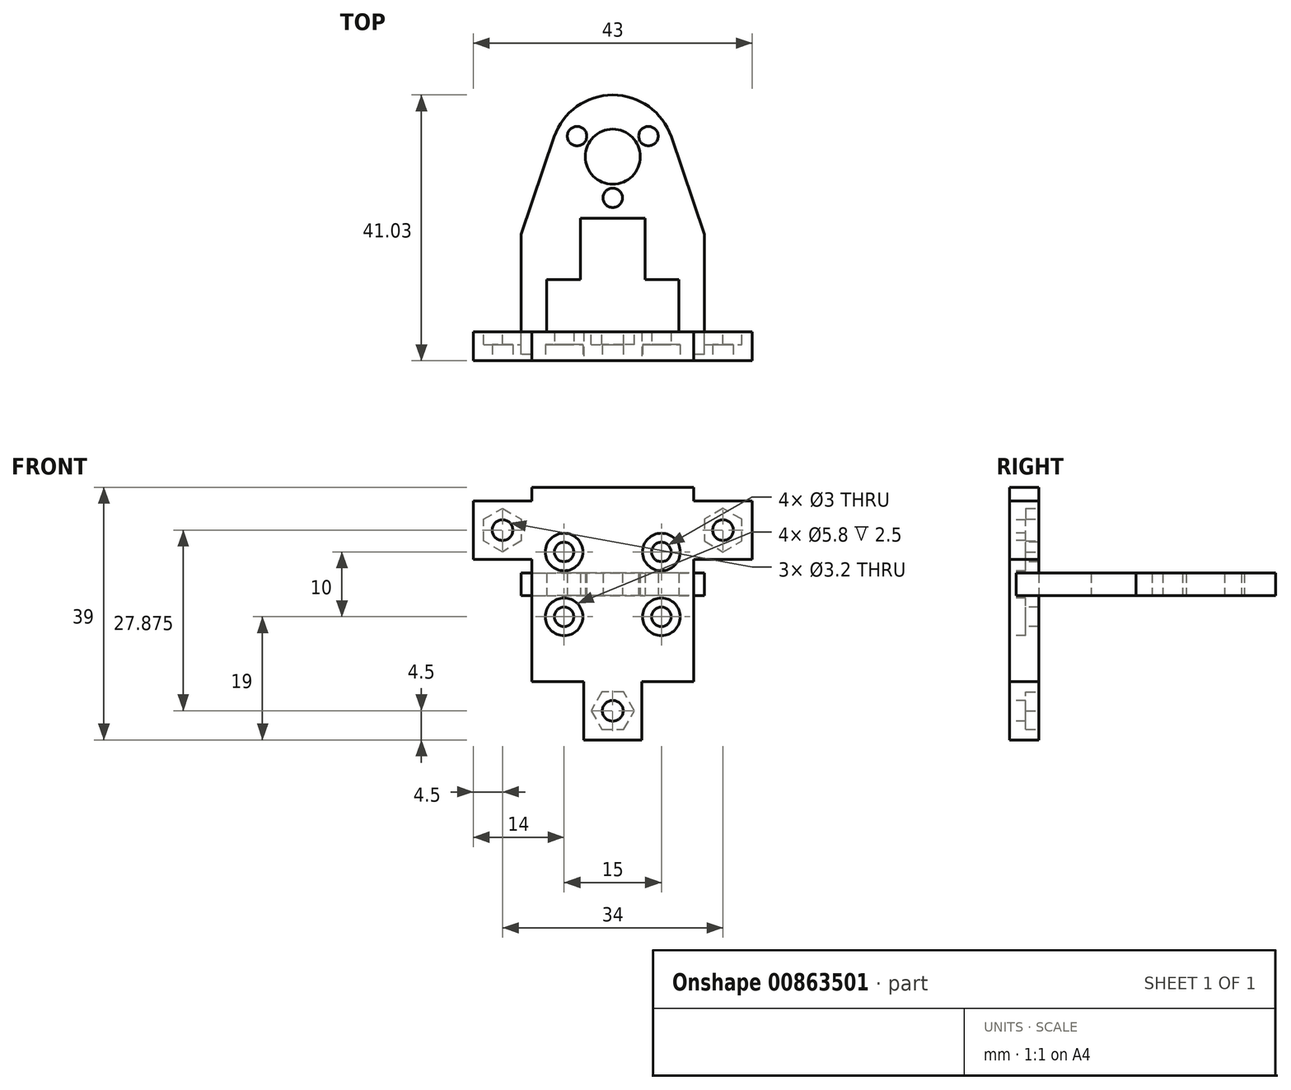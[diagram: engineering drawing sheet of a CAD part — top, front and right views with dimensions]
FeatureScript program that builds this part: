
annotation { "Feature Type Name" : "Feature", "Feature Type Description" : "" }
export const myFeature = defineFeature(function(context is Context, id is Id, definition is map)
    precondition{}
    {
        {
            var Q0;
            Q0=qCreatedBy(makeId("Top.planeOp"),FACE);
            var sketch = newSketch(context, id + "F0", { "sketchPlane" : qUnion([Q0])});
            skCircle(sketch, "E0", {"center": v(0, 0) * mm, "radius": 4.25 * mm});
            skCircle(sketch, "E1", {"center": v(0, -6.35) * mm, "radius": 1.5 * mm});
            skCircle(sketch, "E2.1.0", {"center": v(5.5, 3.17) * mm, "radius": 1.5 * mm});
            skCircle(sketch, "E2.2.0", {"center": v(-5.5, 3.18) * mm, "radius": 1.5 * mm});
            skLineSegment(sketch, "E3", {"start": v(0, -30.5) * mm, "end": v(14.1, -30.5) * mm});
            skLineSegment(sketch, "E4", {"start": v(14.1, -30.5) * mm, "end": v(14.1, -12) * mm});
            skCircle(sketch, "E5", {"center": v(0, 0) * mm, "radius": 9.53 * mm, "construction": true});
            skLineSegment(sketch, "E6", {"start": v(14.1, -12) * mm, "end": v(9.03, 3.04) * mm});
            skLineSegment(sketch, "E7", {"start": v(0, -27) * mm, "end": v(10.2, -27) * mm});
            skLineSegment(sketch, "E8", {"start": v(10.2, -27) * mm, "end": v(10.2, -18.95) * mm});
            skLineSegment(sketch, "E9", {"start": v(10.2, -18.95) * mm, "end": v(5, -18.95) * mm});
            skLineSegment(sketch, "E10", {"start": v(5, -18.95) * mm, "end": v(5, -9.52) * mm});
            skLineSegment(sketch, "E11", {"start": v(5, -9.52) * mm, "end": v(0, -9.52) * mm});
            skLineSegment(sketch, "E12.MirrorCS", {"start": v(-14.1, -12) * mm, "end": v(-9.03, 3.04) * mm});
            skLineSegment(sketch, "E13.MirrorCS", {"start": v(-5, -18.95) * mm, "end": v(-5, -9.52) * mm});
            skLineSegment(sketch, "E14.MirrorCS", {"start": v(-5, -9.52) * mm, "end": v(0, -9.52) * mm});
            skLineSegment(sketch, "E15.MirrorCS", {"start": v(-10.2, -18.95) * mm, "end": v(-5, -18.95) * mm});
            skLineSegment(sketch, "E16.MirrorCS", {"start": v(-10.2, -27) * mm, "end": v(-10.2, -18.95) * mm});
            skLineSegment(sketch, "E17.MirrorCS", {"start": v(0, -27) * mm, "end": v(-10.2, -27) * mm});
            skLineSegment(sketch, "E18.MirrorCS", {"start": v(-14.1, -30.5) * mm, "end": v(-14.1, -12) * mm});
            skLineSegment(sketch, "E19.MirrorCS", {"start": v(0, -30.5) * mm, "end": v(-14.1, -30.5) * mm});
            skArc(sketch, "E20", {"start": v(9.03, 3.04) * mm, "mid": v(0, 9.53) * mm, "end": v(-9.03, 3.04) * mm});
            skSolve(sketch);
        }
        {
            var Q0;
            Q0=makeQuery(id+"F0.imprint","IMPRINT",FACE,{"disambiguationData":[TD([[makeQuery(id+"F0.imprint","IMPRINT",EDGE,{"derivedFrom":sQuery(id+"F0.wireOp",EDGE,"E0")}),-1.0]])]});
            extrude(context, id + "F1", {"entities" : qUnion([Q0]), "depth" : 3.5 * mm, "offsetDistance" : 25 * mm});
        }
        {
            var Q0;
            Q0=makeQuery(id+"F1.opExtrude","SWEPT_FACE",FACE,{"disambiguationData":[OSD([sQuery(id+"F0.wireOp",EDGE,"E3"),sQuery(id+"F0.wireOp",EDGE,"E19.MirrorCS")])]});
            var sketch = newSketch(context, id + "F2", { "sketchPlane" : qUnion([Q0])});
            skLineSegment(sketch, "E21.bottom", {"start": v(-12.5, 16.75) * mm, "end": v(12.5, 16.75) * mm});
            skLineSegment(sketch, "E21.top", {"start": v(-12.5, -13.25) * mm, "end": v(12.5, -13.25) * mm});
            skLineSegment(sketch, "E21.left", {"start": v(-12.5, 16.75) * mm, "end": v(-12.5, -13.25) * mm});
            skLineSegment(sketch, "E21.right", {"start": v(12.5, 16.75) * mm, "end": v(12.5, -13.25) * mm});
            skPoint(sketch, "E21.middle", {"position": v(0, 1.75) * mm});
            skPoint(sketch, "E21.middle.positionSnap0", {"position": v(14.1, 1.75) * mm});
            skPoint(sketch, "E21.centerSnap0", {"position": v(14.1, 1.75) * mm});
            skCircle(sketch, "E22", {"center": v(-7.5, -3.25) * mm, "radius": 1.5 * mm});
            skCircle(sketch, "E23", {"center": v(-7.5, 6.75) * mm, "radius": 1.5 * mm});
            skCircle(sketch, "E24", {"center": v(7.5, 6.75) * mm, "radius": 1.5 * mm});
            skCircle(sketch, "E25", {"center": v(7.5, -3.25) * mm, "radius": 1.5 * mm});
            skLineSegment(sketch, "E26.bottom", {"start": v(-12.5, 5.62) * mm, "end": v(-21.5, 5.62) * mm});
            skLineSegment(sketch, "E26.top", {"start": v(-12.5, 14.62) * mm, "end": v(-21.5, 14.62) * mm});
            skLineSegment(sketch, "E26.left", {"start": v(-12.5, 5.63) * mm, "end": v(-12.5, 14.62) * mm});
            skLineSegment(sketch, "E26.right", {"start": v(-21.5, 5.62) * mm, "end": v(-21.5, 14.63) * mm});
            skLineSegment(sketch, "E27", {"start": v(0, 1.75) * mm, "end": v(0, 16.75) * mm, "construction": true});
            skLineSegment(sketch, "E28", {"start": v(0, 1.75) * mm, "end": v(14.1, 1.75) * mm, "construction": true});
            skLineSegment(sketch, "E29.MirrorCS", {"start": v(12.5, 14.63) * mm, "end": v(21.5, 14.63) * mm});
            skLineSegment(sketch, "E30.MirrorCS", {"start": v(21.5, 5.63) * mm, "end": v(21.5, 14.63) * mm});
            skLineSegment(sketch, "E31.MirrorCS", {"start": v(12.5, 5.63) * mm, "end": v(21.5, 5.63) * mm});
            skCircle(sketch, "E32", {"center": v(-17, 10.12) * mm, "radius": 1.6 * mm});
            skPoint(sketch, "E32.centerSnap0", {"position": v(-12.5, 10.12) * mm});
            skCircle(sketch, "E33.MirrorC", {"center": v(17, 10.13) * mm, "radius": 1.6 * mm});
            skLineSegment(sketch, "E34.bottom", {"start": v(-4.5, -13.25) * mm, "end": v(4.5, -13.25) * mm});
            skLineSegment(sketch, "E34.top", {"start": v(-4.5, -22.25) * mm, "end": v(4.5, -22.25) * mm});
            skLineSegment(sketch, "E34.left", {"start": v(-4.5, -13.25) * mm, "end": v(-4.5, -22.25) * mm});
            skLineSegment(sketch, "E34.right", {"start": v(4.5, -13.25) * mm, "end": v(4.5, -22.25) * mm});
            skCircle(sketch, "E35", {"center": v(0, -17.75) * mm, "radius": 1.6 * mm});
            skPoint(sketch, "E35.centerSnap0", {"position": v(4.5, -17.75) * mm});
            skSolve(sketch);
        }
        {
            var Q0;
            {var subQ1=sQuery(id+"F2.wireOp",EDGE,"E21.bottom");Q0=makeQuery(id+"F2.imprint","IMPRINT",FACE,{"disambiguationData":[TD([[makeQuery(id+"F2.imprint","IMPRINT",EDGE,{"derivedFrom":subQ1}),-1.0]])]});}
            var Q1;
            {var subQ1=sQuery(id+"F2.wireOp",EDGE,"E21.top");Q1=makeQuery(id+"F2.imprint","IMPRINT",FACE,{"disambiguationData":[TD([[makeQuery(id+"F2.imprint","IMPRINT",EDGE,{"derivedFrom":subQ1}),1.0]])]});}
            var Q2;
            {var subQ0=sQuery(id+"F2.wireOp",EDGE,"E26.bottom");Q2=makeQuery(id+"F2.imprint","IMPRINT",FACE,{"disambiguationData":[TD([[makeQuery(id+"F2.imprint","IMPRINT",EDGE,{"derivedFrom":subQ0}),-1.0]])]});}
            var Q3;
            {var subQ2=sQuery(id+"F2.wireOp",EDGE,"E29.MirrorCS");Q3=makeQuery(id+"F2.imprint","IMPRINT",FACE,{"disambiguationData":[TD([[makeQuery(id+"F2.imprint","IMPRINT",EDGE,{"derivedFrom":subQ2}),-1.0]])]});}
            var Q4;
            Q4=makeQuery(id+"F2.imprint","IMPRINT",FACE,{"disambiguationData":[TD([[makeQuery(id+"F2.imprint","IMPRINT",EDGE,{"derivedFrom":sQuery(id+"F2.wireOp",EDGE,"E34.top")}),1.0]])]});
            var Q5;
            Q5=makeQuery(id+"F2.imprint","IMPRINT",FACE,{"disambiguationData":[TD([[makeQuery(id+"F2.imprint","IMPRINT",EDGE,{"derivedFrom":sQuery(id+"F2.wireOp",EDGE,"E32")}),-1.0]])]});
            var Q6;
            Q6=makeQuery(id+"F2.imprint","IMPRINT",FACE,{"disambiguationData":[TD([[makeQuery(id+"F2.imprint","IMPRINT",EDGE,{"derivedFrom":sQuery(id+"F2.wireOp",EDGE,"978b7f84-c101-4c4e-b361-f8c2110946930.MirrorC")}),-1.0]])]});
            var Q7;
            Q7=makeQuery(id+"F2.imprint","IMPRINT",FACE,{"disambiguationData":[TD([[makeQuery(id+"F2.imprint","IMPRINT",EDGE,{"derivedFrom":sQuery(id+"F2.wireOp",EDGE,"E35")}),-1.0]])]});
            var Q8;
            {var subQ0=sQuery(id+"F2.wireOp",EDGE,"E21.left");var subQ1=sQuery(id+"F0.wireOp",EDGE,"E19.MirrorCS");var subQ2=sQuery(id+"F0.wireOp",EDGE,"E3");var subQ3=makeQuery(id+"F1.opExtrude","CAP_EDGE",EDGE,{"disambiguationData":[OSD([subQ2,subQ1])],"isStart":false});var subQ4=makeQuery(id+"F2.imprint","INTERSECT",VERTEX,{"derivedFrom":[subQ3,subQ0]});Q8=makeQuery(id+"F2.imprint","IMPRINT",FACE,{"disambiguationData":[TD([[makeQuery(id+"F2.imprint","IMPRINT",EDGE,{"disambiguationData":[TD([[subQ4,-1.0]])],"derivedFrom":subQ0}),1.0]])]});}
            extrude(context, id + "F3", {"entities" : qUnion([Q0, Q1, Q2, Q3, Q4, Q5, Q6, Q7, Q8]), "operationType" : NewBodyOperationType.ADD, "oppositeDirection" : true, "depth" : 3.5 * mm, "offsetDistance" : 25 * mm, "hasSecondDirection" : true, "secondDirectionOppositeDirection" : false, "secondDirectionDepth" : 1 * mm});
        }
        {
            var Q0;
            Q0=makeQuery(id+"F3.boolean.opBoolean","MERGE",FACE,{"derivedFrom":[makeQuery(id+"F1.opExtrude","SWEPT_FACE",FACE,{"disambiguationData":[OSD([sQuery(id+"F0.wireOp",EDGE,"E7"),sQuery(id+"F0.wireOp",EDGE,"E17.MirrorCS")])]}),makeQuery(id+"F3.opExtrude","CAP_FACE",FACE,{"disambiguationData":[OSD([sQuery(id+"F2.wireOp",EDGE,"E21.bottom"),sQuery(id+"F2.wireOp",EDGE,"E21.top"),sQuery(id+"F2.wireOp",EDGE,"E21.left"),sQuery(id+"F2.wireOp",EDGE,"E21.right"),sQuery(id+"F2.wireOp",EDGE,"E22"),sQuery(id+"F2.wireOp",EDGE,"E23"),sQuery(id+"F2.wireOp",EDGE,"E24"),sQuery(id+"F2.wireOp",EDGE,"E25"),sQuery(id+"F2.wireOp",EDGE,"E26.bottom"),sQuery(id+"F2.wireOp",EDGE,"E26.top"),sQuery(id+"F2.wireOp",EDGE,"E26.right"),sQuery(id+"F2.wireOp",EDGE,"E29.MirrorCS"),sQuery(id+"F2.wireOp",EDGE,"E30.MirrorCS"),sQuery(id+"F2.wireOp",EDGE,"E31.MirrorCS"),sQuery(id+"F2.wireOp",EDGE,"E32"),sQuery(id+"F2.wireOp",EDGE,"E33.MirrorC"),sQuery(id+"F2.wireOp",EDGE,"E34.top"),sQuery(id+"F2.wireOp",EDGE,"E34.left"),sQuery(id+"F2.wireOp",EDGE,"E34.right"),sQuery(id+"F2.wireOp",EDGE,"E35")])],"isStart":false})]});
            var sketch = newSketch(context, id + "F4", { "sketchPlane" : qUnion([Q0])});
            skCircle(sketch, "E36.cCircle", {"center": v(-17, 10.13) * mm, "radius": 2.9 * mm, "construction": true});
            skLineSegment(sketch, "E36.0", {"start": v(-19.9, 8.45) * mm, "end": v(-19.9, 11.8) * mm});
            skLineSegment(sketch, "E36.1", {"start": v(-19.9, 11.8) * mm, "end": v(-17, 13.47) * mm});
            skLineSegment(sketch, "E36.2", {"start": v(-17, 13.47) * mm, "end": v(-14.1, 11.8) * mm});
            skLineSegment(sketch, "E36.3", {"start": v(-14.1, 11.8) * mm, "end": v(-14.1, 8.45) * mm});
            skLineSegment(sketch, "E36.4", {"start": v(-14.1, 8.45) * mm, "end": v(-17, 6.78) * mm});
            skLineSegment(sketch, "E36.5", {"start": v(-17, 6.78) * mm, "end": v(-19.9, 8.45) * mm});
            skPoint(sketch, "E36.0.midPoint", {"position": v(-19.9, 10.13) * mm});
            skPoint(sketch, "E37.MirrorP", {"position": v(19.9, 10.13) * mm});
            skLineSegment(sketch, "E38.MirrorCS", {"start": v(14.1, 11.8) * mm, "end": v(14.1, 8.45) * mm});
            skLineSegment(sketch, "E39.MirrorCS", {"start": v(19.9, 8.45) * mm, "end": v(19.9, 11.8) * mm});
            skLineSegment(sketch, "E40.MirrorCS", {"start": v(17, 6.78) * mm, "end": v(19.9, 8.45) * mm});
            skCircle(sketch, "E41.MirrorC", {"center": v(17, 10.13) * mm, "radius": 2.9 * mm, "construction": true});
            skLineSegment(sketch, "E42.MirrorCS", {"start": v(17, 13.47) * mm, "end": v(14.1, 11.8) * mm});
            skLineSegment(sketch, "E43.MirrorCS", {"start": v(19.9, 11.8) * mm, "end": v(17, 13.47) * mm});
            skLineSegment(sketch, "E44.MirrorCS", {"start": v(14.1, 8.45) * mm, "end": v(17, 6.78) * mm});
            skCircle(sketch, "E45.cCircle", {"center": v(0, -17.75) * mm, "radius": 2.9 * mm, "construction": true});
            skLineSegment(sketch, "E45.0", {"start": v(-1.67, -14.85) * mm, "end": v(1.67, -14.85) * mm});
            skLineSegment(sketch, "E45.1", {"start": v(1.67, -14.85) * mm, "end": v(3.35, -17.75) * mm});
            skLineSegment(sketch, "E45.2", {"start": v(3.35, -17.75) * mm, "end": v(1.67, -20.65) * mm});
            skLineSegment(sketch, "E45.3", {"start": v(1.67, -20.65) * mm, "end": v(-1.67, -20.65) * mm});
            skLineSegment(sketch, "E45.4", {"start": v(-1.67, -20.65) * mm, "end": v(-3.35, -17.75) * mm});
            skLineSegment(sketch, "E45.5", {"start": v(-3.35, -17.75) * mm, "end": v(-1.67, -14.85) * mm});
            skPoint(sketch, "E45.0.midPoint", {"position": v(0, -14.85) * mm});
            skSolve(sketch);
        }
        {
            var Q0;
            Q0=makeQuery(id+"F4.imprint","IMPRINT",FACE,{"disambiguationData":[TD([[makeQuery(id+"F4.imprint","IMPRINT",EDGE,{"derivedFrom":sQuery(id+"F4.wireOp",EDGE,"E36.0")}),-1.0]])]});
            var Q1;
            Q1=makeQuery(id+"F4.imprint","IMPRINT",FACE,{"disambiguationData":[TD([[makeQuery(id+"F4.imprint","IMPRINT",EDGE,{"derivedFrom":sQuery(id+"F4.wireOp",EDGE,"E38.MirrorCS")}),1.0]])]});
            var Q2;
            Q2=makeQuery(id+"F4.imprint","IMPRINT",FACE,{"disambiguationData":[TD([[makeQuery(id+"F4.imprint","IMPRINT",EDGE,{"derivedFrom":sQuery(id+"F4.wireOp",EDGE,"E45.0")}),-1.0]])]});
            extrude(context, id + "F5", {"entities" : qUnion([Q0, Q1, Q2]), "operationType" : NewBodyOperationType.REMOVE, "oppositeDirection" : true, "depth" : 2 * mm, "offsetDistance" : 25 * mm});
        }
        {
            var Q0;
            Q0=makeQuery(id+"F3.opExtrude","CAP_FACE",FACE,{"disambiguationData":[OSD([sQuery(id+"F2.wireOp",EDGE,"E21.bottom"),sQuery(id+"F2.wireOp",EDGE,"E21.top"),sQuery(id+"F2.wireOp",EDGE,"E21.left"),sQuery(id+"F2.wireOp",EDGE,"E21.right"),sQuery(id+"F2.wireOp",EDGE,"E22"),sQuery(id+"F2.wireOp",EDGE,"E23"),sQuery(id+"F2.wireOp",EDGE,"E24"),sQuery(id+"F2.wireOp",EDGE,"E25"),sQuery(id+"F2.wireOp",EDGE,"E26.bottom"),sQuery(id+"F2.wireOp",EDGE,"E26.top"),sQuery(id+"F2.wireOp",EDGE,"E26.right"),sQuery(id+"F2.wireOp",EDGE,"E29.MirrorCS"),sQuery(id+"F2.wireOp",EDGE,"E30.MirrorCS"),sQuery(id+"F2.wireOp",EDGE,"E31.MirrorCS"),sQuery(id+"F2.wireOp",EDGE,"E32"),sQuery(id+"F2.wireOp",EDGE,"E33.MirrorC"),sQuery(id+"F2.wireOp",EDGE,"E34.top"),sQuery(id+"F2.wireOp",EDGE,"E34.left"),sQuery(id+"F2.wireOp",EDGE,"E34.right"),sQuery(id+"F2.wireOp",EDGE,"E35")])],"isStart":true});
            var sketch = newSketch(context, id + "F6", { "sketchPlane" : qUnion([Q0])});
            skCircle(sketch, "E46", {"center": v(-7.5, 6.75) * mm, "radius": 2.9 * mm});
            skCircle(sketch, "E47", {"center": v(7.5, 6.75) * mm, "radius": 2.9 * mm});
            skCircle(sketch, "E48", {"center": v(7.5, -3.25) * mm, "radius": 2.9 * mm});
            skCircle(sketch, "E49", {"center": v(-7.5, -3.25) * mm, "radius": 2.9 * mm});
            skSolve(sketch);
        }
        {
            var Q0;
            Q0=makeQuery(id+"F6.imprint","IMPRINT",FACE,{"disambiguationData":[TD([[makeQuery(id+"F6.imprint","IMPRINT",EDGE,{"derivedFrom":sQuery(id+"F6.wireOp",EDGE,"E46")}),1.0]])]});
            var Q1;
            Q1=makeQuery(id+"F6.imprint","IMPRINT",FACE,{"disambiguationData":[TD([[makeQuery(id+"F6.imprint","IMPRINT",EDGE,{"derivedFrom":sQuery(id+"F6.wireOp",EDGE,"E47")}),1.0]])]});
            var Q2;
            Q2=makeQuery(id+"F6.imprint","IMPRINT",FACE,{"disambiguationData":[TD([[makeQuery(id+"F6.imprint","IMPRINT",EDGE,{"derivedFrom":sQuery(id+"F6.wireOp",EDGE,"E48")}),1.0]])]});
            var Q3;
            Q3=makeQuery(id+"F6.imprint","IMPRINT",FACE,{"disambiguationData":[TD([[makeQuery(id+"F6.imprint","IMPRINT",EDGE,{"derivedFrom":sQuery(id+"F6.wireOp",EDGE,"E49")}),1.0]])]});
            extrude(context, id + "F7", {"entities" : qUnion([Q0, Q1, Q2, Q3]), "operationType" : NewBodyOperationType.REMOVE, "oppositeDirection" : true, "depth" : 2.5 * mm, "offsetDistance" : 25 * mm});
        }
    });
